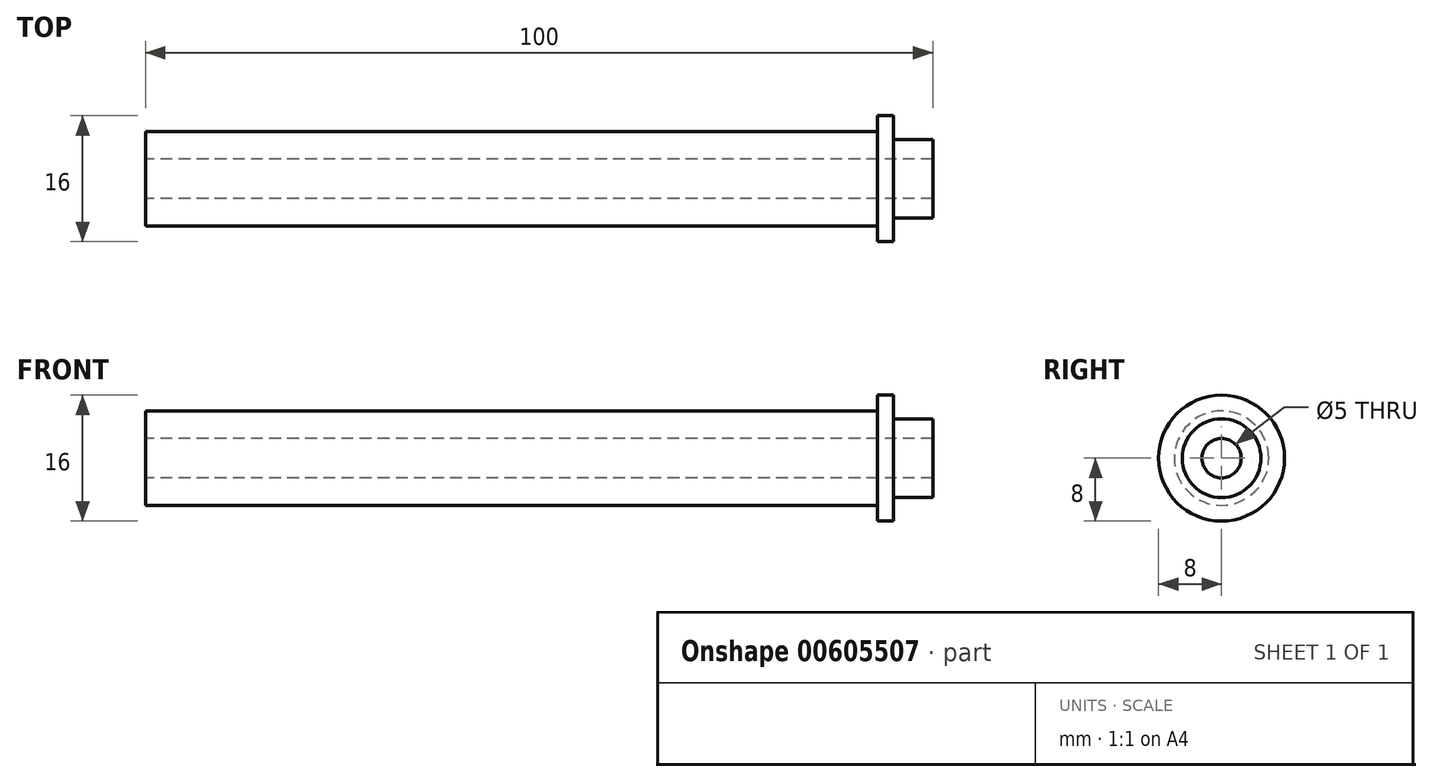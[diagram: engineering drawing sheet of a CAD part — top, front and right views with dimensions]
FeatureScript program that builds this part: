
annotation { "Feature Type Name" : "Feature", "Feature Type Description" : "" }
export const myFeature = defineFeature(function(context is Context, id is Id, definition is map)
    precondition{}
    {
        {
            var Q0;
            Q0=qCreatedBy(makeId("Front.planeOp"),FACE);
            var sketch = newSketch(context, id + "F0", { "sketchPlane" : qUnion([Q0])});
            skLineSegment(sketch, "E0.bottom", {"start": v(-35.86, 28.27) * mm, "end": v(57.14, 28.27) * mm});
            skLineSegment(sketch, "E0.top", {"start": v(-35.86, 31.77) * mm, "end": v(57.14, 31.77) * mm});
            skLineSegment(sketch, "E0.left", {"start": v(-35.86, 28.27) * mm, "end": v(-35.86, 31.77) * mm});
            skLineSegment(sketch, "E0.right", {"start": v(57.14, 28.27) * mm, "end": v(57.14, 31.77) * mm});
            skLineSegment(sketch, "E1.bottom", {"start": v(57.14, 28.27) * mm, "end": v(59.14, 28.27) * mm});
            skLineSegment(sketch, "E1.top", {"start": v(57.14, 33.77) * mm, "end": v(59.14, 33.77) * mm});
            skLineSegment(sketch, "E1.left", {"start": v(57.14, 28.27) * mm, "end": v(57.14, 33.77) * mm});
            skLineSegment(sketch, "E1.right", {"start": v(59.14, 28.27) * mm, "end": v(59.14, 33.77) * mm});
            skLineSegment(sketch, "E2.bottom", {"start": v(59.14, 28.27) * mm, "end": v(64.14, 28.27) * mm});
            skLineSegment(sketch, "E2.top", {"start": v(59.14, 30.77) * mm, "end": v(64.14, 30.77) * mm});
            skLineSegment(sketch, "E2.left", {"start": v(59.14, 28.27) * mm, "end": v(59.14, 30.77) * mm});
            skLineSegment(sketch, "E2.right", {"start": v(64.14, 28.27) * mm, "end": v(64.14, 30.77) * mm});
            skLineSegment(sketch, "E3", {"start": v(-46.08, 25.77) * mm, "end": v(65.78, 25.77) * mm, "construction": true});
            skSolve(sketch);
        }
        {
            var Q0;
            {var subQ0=sQuery(id+"F0.wireOp",EDGE,"E0.bottom");Q0=makeQuery(id+"F0.imprint","IMPRINT",FACE,{"disambiguationData":[TD([[makeQuery(id+"F0.imprint","IMPRINT",EDGE,{"derivedFrom":subQ0}),1.0]])]});}
            var Q1;
            {var subQ3=sQuery(id+"F0.wireOp",EDGE,"E1.bottom");Q1=makeQuery(id+"F0.imprint","IMPRINT",FACE,{"disambiguationData":[TD([[makeQuery(id+"F0.imprint","IMPRINT",EDGE,{"derivedFrom":subQ3}),1.0]])]});}
            var Q2;
            Q2=makeQuery(id+"F0.imprint","IMPRINT",FACE,{"disambiguationData":[TD([[makeQuery(id+"F0.imprint","IMPRINT",EDGE,{"derivedFrom":sQuery(id+"F0.wireOp",EDGE,"E2.bottom")}),1.0]])]});
            var Q3;
            Q3=sQuery(id+"F0.wireOp",EDGE,"E3");
            revolve(context, id + "F1", {"entities" : qUnion([Q0, Q1, Q2]), "axis" : qUnion([Q3]), "revolveType" : RevolveType.FULL});
        }
    });
